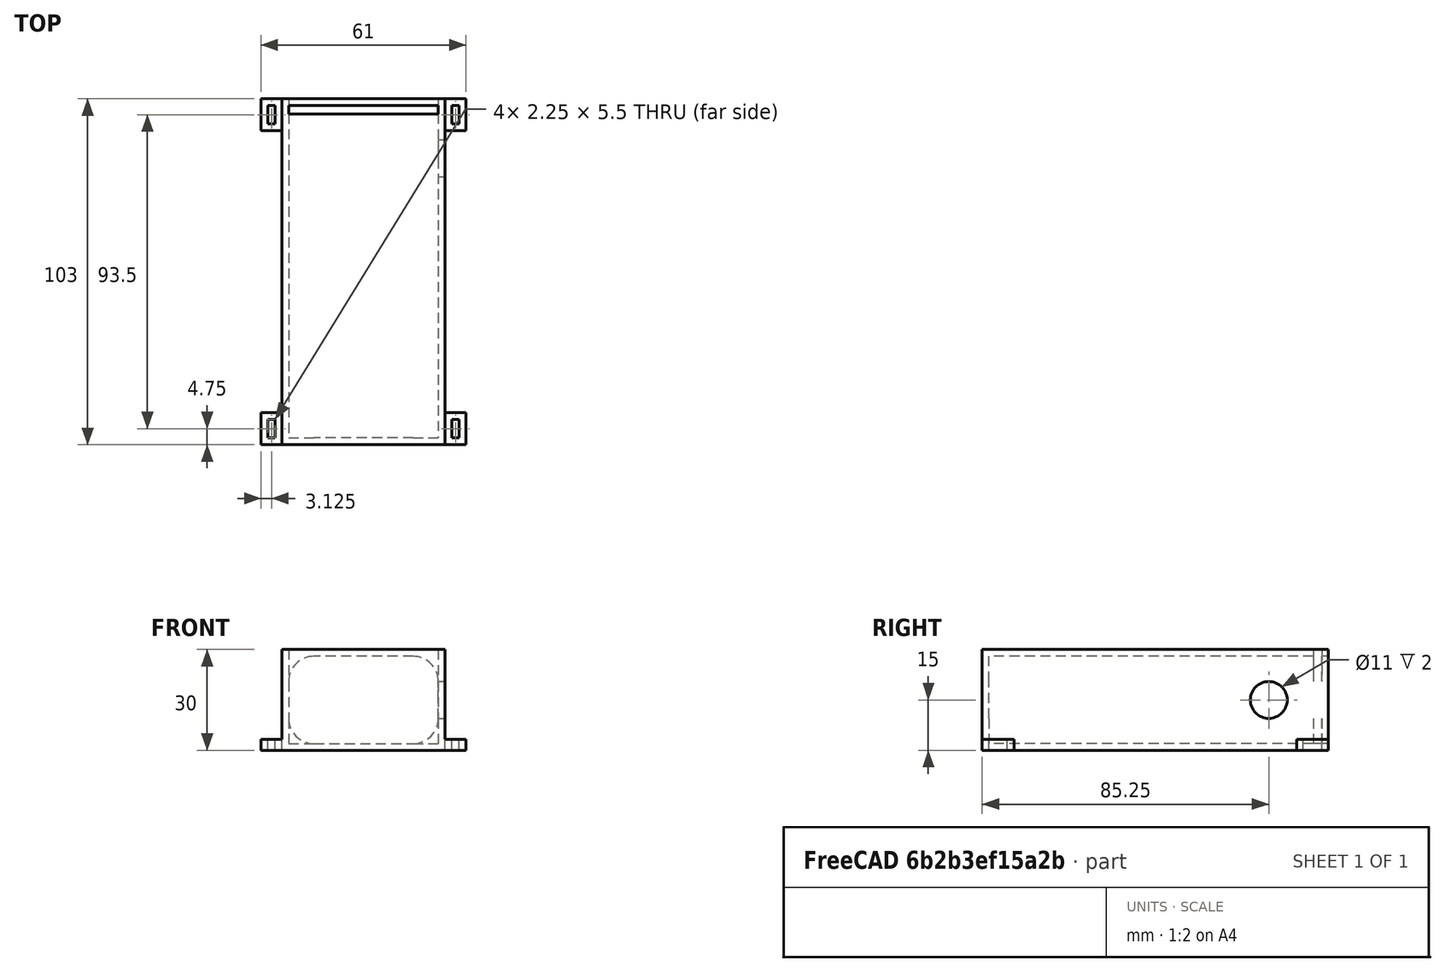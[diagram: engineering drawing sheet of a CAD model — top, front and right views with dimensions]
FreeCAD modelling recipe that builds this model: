
FCSTD DOCUMENT  (FreeCAD 0.19R)
Label: power-bank-mount-base
License: All rights reserved
LicenseURL: http://en.wikipedia.org/wiki/All_rights_reserved
objects: Sketcher::SketchObject×5, PartDesign::Pocket×3, PartDesign::Pad×2, PartDesign::Body×1, Mesh::Feature×1
note: 16 computed .brp shape members not serialized (recipe doc carries the construction recipe); baked Part::Feature solids carry a one-line shape summary decoded from their .brp

FEATURE [Sketcher::SketchObject] Sketch
  FullyConstrained = true
  MapMode = 5
  Support = -> [XY_Plane]
  sketch-geometry (4):
    g0: LineSegment StartX=0 StartY=0 StartZ=0 EndX=48.5 EndY=0 EndZ=0
    g1: LineSegment StartX=48.5 StartY=0 StartZ=0 EndX=48.5 EndY=103 EndZ=0
    g2: LineSegment StartX=48.5 StartY=103 StartZ=0 EndX=0 EndY=103 EndZ=0
    g3: LineSegment StartX=0 StartY=103 StartZ=0 EndX=0 EndY=0 EndZ=0
  constraints (11):
    c: Coincident(g0,g1)
    c: Coincident(g1,g2)
    c: Coincident(g2,g3)
    c: Coincident(g3,g0)
    c: Horizontal(g0)
    c: Horizontal(g2)
    c: Vertical(g1)
    c: Vertical(g3)
    c: Coincident(g0,g-1)
    c: DistanceX(g2,g2) = 48.5
    c: DistanceY(g1,g1) = 103
FEATURE [PartDesign::Pad] Pad
  Direction = (1,1,1)
  Length = 30
  Length2 = 100
  Profile = -> Sketch
  Type = 0
FEATURE [Sketcher::SketchObject] Sketch001
  FullyConstrained = true
  MapMode = 5
  Placement = pos=(0,103,0) rot=(0,0.707107,0.707107;3.14159rad)
  Support = -> [Pad]
  sketch-geometry (14):
    g0: LineSegment StartX=-39 StartY=28 StartZ=0 EndX=-9.5 EndY=28 EndZ=0
    g1: LineSegment StartX=-2 StartY=20.5 StartZ=0 EndX=-2 EndY=9.5 EndZ=0
    g2: LineSegment StartX=-9.5 StartY=2 StartZ=0 EndX=-39 EndY=2 EndZ=0
    g3: LineSegment StartX=-46.5 StartY=9.5 StartZ=0 EndX=-46.5 EndY=20.5 EndZ=0
    g4: ArcOfCircle CenterX=-39 CenterY=20.5 CenterZ=0 NormalX=0 NormalY=0 NormalZ=1 AngleXU=0 Radius=7.5 StartAngle=1.5708 EndAngle=3.14159
    g5: ArcOfCircle CenterX=-9.5 CenterY=20.5 CenterZ=0 NormalX=0 NormalY=0 NormalZ=1 AngleXU=0 Radius=7.5 StartAngle=0 EndAngle=1.5708
    g6: ArcOfCircle CenterX=-9.5 CenterY=9.5 CenterZ=0 NormalX=0 NormalY=0 NormalZ=1 AngleXU=0 Radius=7.5 StartAngle=4.71239 EndAngle=6.28319
    g7: ArcOfCircle CenterX=-39 CenterY=9.5 CenterZ=0 NormalX=0 NormalY=0 NormalZ=1 AngleXU=0 Radius=7.5 StartAngle=3.14159 EndAngle=4.71239
    g8: LineSegment StartX=0 StartY=0 StartZ=0 EndX=-48.5 EndY=0 EndZ=0
    g9: LineSegment StartX=-48.5 StartY=0 StartZ=0 EndX=-48.5 EndY=30 EndZ=0
    g10: LineSegment StartX=-48.5 StartY=30 StartZ=0 EndX=0 EndY=30 EndZ=0
    g11: LineSegment StartX=0 StartY=30 StartZ=0 EndX=0 EndY=0 EndZ=0
    g12: LineSegment StartX=-24.25 StartY=28 StartZ=0 EndX=-24.25 EndY=30 EndZ=0
    g13: LineSegment StartX=-2 StartY=15 StartZ=0 EndX=0 EndY=15 EndZ=0
  constraints (35):
    c: Horizontal(g0)
    c: Horizontal(g2)
    c: Vertical(g1)
    c: Vertical(g3)
    c: Tangent(g0,g4) = 1.5708
    c: Tangent(g3,g4) = 1.5708
    c: Tangent(g0,g5) = 1.5708
    c: Tangent(g1,g5) = 1.5708
    c: Tangent(g1,g6) = 1.5708
    c: Tangent(g2,g6) = 1.5708
    c: Tangent(g2,g7) = 1.5708
    c: Tangent(g3,g7) = 1.5708
    c: DistanceY(g2,g0) = 26
    c: Coincident(g8,g9)
    c: Coincident(g9,g10)
    c: Coincident(g10,g11)
    c: Coincident(g11,g8)
    c: Horizontal(g8)
    c: Horizontal(g10)
    c: Vertical(g9)
    c: Vertical(g11)
    c: Coincident(g8,g-1)
    c: DistanceX(g10,g10) = 48.5
    c: DistanceY(g9,g9) = 30
    c: Distance(g0,g5) = 7.5
    c: Equal(g5,g4)
    c: Equal(g4,g7)
    c: Equal(g7,g6)
    c: Vertical(g12)
    c: Horizontal(g13)
    c: DistanceX(g3,g1) = 44.5
    c: Symmetric(g10,g9,g12)
    c: Symmetric(g0,g0,g12)
    c: Symmetric(g1,g1,g13)
    c: Symmetric(g-1,g10,g13)
FEATURE [PartDesign::Pocket] Pocket
  BaseFeature = -> Pad
  Length = 101
  Length2 = 100
  Profile = -> Sketch001
  Type = 0
FEATURE [Sketcher::SketchObject] Sketch002
  FullyConstrained = true
  MapMode = 5
  Placement = pos=(0,0,30) rot=(0,0,1;0rad)
  Support = -> [Pocket]
  sketch-geometry (9):
    g0: LineSegment StartX=0 StartY=0 StartZ=0 EndX=48.5 EndY=0 EndZ=0
    g1: LineSegment StartX=48.5 StartY=0 StartZ=0 EndX=48.5 EndY=103 EndZ=0
    g2: LineSegment StartX=48.5 StartY=103 StartZ=0 EndX=0 EndY=103 EndZ=0
    g3: LineSegment StartX=0 StartY=103 StartZ=0 EndX=0 EndY=0 EndZ=0
    g4: LineSegment StartX=2 StartY=101 StartZ=0 EndX=46.5 EndY=101 EndZ=0
    g5: LineSegment StartX=46.5 StartY=101 StartZ=0 EndX=46.5 EndY=98.5 EndZ=0
    g6: LineSegment StartX=46.5 StartY=98.5 StartZ=0 EndX=2 EndY=98.5 EndZ=0
    g7: LineSegment StartX=2 StartY=98.5 StartZ=0 EndX=2 EndY=101 EndZ=0
    g8: LineSegment StartX=24.25 StartY=101 StartZ=0 EndX=24.25 EndY=103 EndZ=0
  constraints (25):
    c: Coincident(g0,g1)
    c: Coincident(g1,g2)
    c: Coincident(g2,g3)
    c: Coincident(g3,g0)
    c: Horizontal(g0)
    c: Horizontal(g2)
    c: Vertical(g1)
    c: Vertical(g3)
    c: Coincident(g0,g-1)
    c: Coincident(g4,g5)
    c: Coincident(g5,g6)
    c: Coincident(g6,g7)
    c: Coincident(g7,g4)
    c: Horizontal(g4)
    c: Horizontal(g6)
    c: Vertical(g5)
    c: Vertical(g7)
    c: Vertical(g8)
    c: DistanceX(g0,g0) = 48.5
    c: DistanceY(g1,g1) = 103
    c: DistanceX(g6,g6) = 44.5
    c: DistanceY(g5,g5) = 2.5
    c: Symmetric(g4,g4,g8)
    c: Symmetric(g1,g2,g8)
    c: DistanceY(g8,g8) = 2
FEATURE [PartDesign::Pocket] Pocket001
  BaseFeature = -> Pocket
  Length = 28
  Length2 = 100
  Profile = -> Sketch002
  Type = 0
FEATURE [Sketcher::SketchObject] Sketch003
  FullyConstrained = true
  MapMode = 5
  Support = -> [XY_Plane]
  sketch-geometry (44):
    g0: LineSegment StartX=0 StartY=0 StartZ=0 EndX=48.5 EndY=0 EndZ=0
    g1: LineSegment StartX=48.5 StartY=0 StartZ=0 EndX=48.5 EndY=103 EndZ=0
    g2: LineSegment StartX=48.5 StartY=103 StartZ=0 EndX=0 EndY=103 EndZ=0
    g3: LineSegment StartX=0 StartY=103 StartZ=0 EndX=0 EndY=0 EndZ=0
    g4: LineSegment StartX=0 StartY=103 StartZ=0 EndX=-6.25 EndY=103 EndZ=0
    g5: LineSegment StartX=-6.25 StartY=103 StartZ=0 EndX=-6.25 EndY=93.5 EndZ=0
    g6: LineSegment StartX=-6.25 StartY=93.5 StartZ=0 EndX=0 EndY=93.5 EndZ=0
    g7: LineSegment StartX=0 StartY=93.5 StartZ=0 EndX=0 EndY=103 EndZ=0
    g8: LineSegment StartX=48.5 StartY=103 StartZ=0 EndX=54.75 EndY=103 EndZ=0
    g9: LineSegment StartX=54.75 StartY=103 StartZ=0 EndX=54.75 EndY=93.5 EndZ=0
    g10: LineSegment StartX=54.75 StartY=93.5 StartZ=0 EndX=48.5 EndY=93.5 EndZ=0
    g11: LineSegment StartX=48.5 StartY=93.5 StartZ=0 EndX=48.5 EndY=103 EndZ=0
    g12: LineSegment StartX=0 StartY=0 StartZ=0 EndX=-6.25 EndY=0 EndZ=0
    g13: LineSegment StartX=-6.25 StartY=0 StartZ=0 EndX=-6.25 EndY=9.5 EndZ=0
    g14: LineSegment StartX=-6.25 StartY=9.5 StartZ=0 EndX=0 EndY=9.5 EndZ=0
    g15: LineSegment StartX=0 StartY=9.5 StartZ=0 EndX=0 EndY=0 EndZ=0
    g16: LineSegment StartX=48.5 StartY=0 StartZ=0 EndX=54.75 EndY=0 EndZ=0
    g17: LineSegment StartX=54.75 StartY=0 StartZ=0 EndX=54.75 EndY=9.5 EndZ=0
    g18: LineSegment StartX=54.75 StartY=9.5 StartZ=0 EndX=48.5 EndY=9.5 EndZ=0
    g19: LineSegment StartX=48.5 StartY=9.5 StartZ=0 EndX=48.5 EndY=0 EndZ=0
    g20: LineSegment StartX=-4.25 StartY=101 StartZ=0 EndX=-2 EndY=101 EndZ=0
    g21: LineSegment StartX=-2 StartY=101 StartZ=0 EndX=-2 EndY=95.5 EndZ=0
    g22: LineSegment StartX=-2 StartY=95.5 StartZ=0 EndX=-4.25 EndY=95.5 EndZ=0
    g23: LineSegment StartX=-4.25 StartY=95.5 StartZ=0 EndX=-4.25 EndY=101 EndZ=0
    g24: LineSegment StartX=50.5 StartY=101 StartZ=0 EndX=52.75 EndY=101 EndZ=0
    g25: LineSegment StartX=52.75 StartY=101 StartZ=0 EndX=52.75 EndY=95.5 EndZ=0
    g26: LineSegment StartX=52.75 StartY=95.5 StartZ=0 EndX=50.5 EndY=95.5 EndZ=0
    g27: LineSegment StartX=50.5 StartY=95.5 StartZ=0 EndX=50.5 EndY=101 EndZ=0
    g28: LineSegment StartX=-4.25 StartY=7.5 StartZ=0 EndX=-2 EndY=7.5 EndZ=0
    g29: LineSegment StartX=-2 StartY=7.5 StartZ=0 EndX=-2 EndY=2 EndZ=0
    g30: LineSegment StartX=-2 StartY=2 StartZ=0 EndX=-4.25 EndY=2 EndZ=0
    g31: LineSegment StartX=-4.25 StartY=2 StartZ=0 EndX=-4.25 EndY=7.5 EndZ=0
    g32: LineSegment StartX=52.75 StartY=7.5 StartZ=0 EndX=50.5 EndY=7.5 EndZ=0
    g33: LineSegment StartX=50.5 StartY=7.5 StartZ=0 EndX=50.5 EndY=2 EndZ=0
    g34: LineSegment StartX=50.5 StartY=2 StartZ=0 EndX=52.75 EndY=2 EndZ=0
    g35: LineSegment StartX=52.75 StartY=2 StartZ=0 EndX=52.75 EndY=7.5 EndZ=0
    g36: LineSegment StartX=-3.125 StartY=101 StartZ=0 EndX=-3.125 EndY=103 EndZ=0
    g37: LineSegment StartX=-4.25 StartY=98.25 StartZ=0 EndX=-6.25 EndY=98.25 EndZ=0
    g38: LineSegment StartX=51.625 StartY=101 StartZ=0 EndX=51.625 EndY=103 EndZ=0
    g39: LineSegment StartX=52.75 StartY=98.25 StartZ=0 EndX=54.75 EndY=98.25 EndZ=0
    g40: LineSegment StartX=-3.125 StartY=7.5 StartZ=0 EndX=-3.125 EndY=9.5 EndZ=0
    g41: LineSegment StartX=-4.25 StartY=4.75 StartZ=0 EndX=-6.25 EndY=4.75 EndZ=0
    g42: LineSegment StartX=51.625 StartY=7.5 StartZ=0 EndX=51.625 EndY=9.5 EndZ=0
    g43: LineSegment StartX=52.75 StartY=4.75 StartZ=0 EndX=54.75 EndY=4.75 EndZ=0
  constraints (119):
    c: Coincident(g0,g1)
    c: Coincident(g1,g2)
    c: Coincident(g2,g3)
    c: Coincident(g3,g0)
    c: Horizontal(g0)
    c: Horizontal(g2)
    c: Vertical(g1)
    c: Vertical(g3)
    c: Coincident(g0,g-1)
    c: DistanceX(g2,g2) = 48.5
    c: DistanceY(g1,g1) = 103
    c: Coincident(g4,g5)
    c: Coincident(g5,g6)
    c: Coincident(g6,g7)
    c: Coincident(g7,g4)
    c: Horizontal(g4)
    c: Horizontal(g6)
    c: Vertical(g5)
    c: Vertical(g7)
    c: Coincident(g4,g2)
    c: Coincident(g8,g9)
    c: Coincident(g9,g10)
    c: Coincident(g10,g11)
    c: Coincident(g11,g8)
    c: Horizontal(g8)
    c: Horizontal(g10)
    c: Vertical(g9)
    c: Vertical(g11)
    c: Coincident(g8,g1)
    c: Coincident(g12,g13)
    c: Coincident(g13,g14)
    c: Coincident(g14,g15)
    c: Coincident(g15,g12)
    c: Horizontal(g12)
    c: Horizontal(g14)
    c: Vertical(g13)
    c: Vertical(g15)
    c: Coincident(g12,g-1)
    c: Coincident(g16,g17)
    c: Coincident(g17,g18)
    c: Coincident(g18,g19)
    c: Coincident(g19,g16)
    c: Horizontal(g16)
    c: Horizontal(g18)
    c: Vertical(g17)
    c: Vertical(g19)
    c: Coincident(g16,g0)
    c: Coincident(g20,g21)
    c: Coincident(g21,g22)
    c: Coincident(g22,g23)
    c: Coincident(g23,g20)
    c: Horizontal(g20)
    c: Horizontal(g22)
    c: Vertical(g21)
    c: Vertical(g23)
    c: Coincident(g24,g25)
    c: Coincident(g25,g26)
    c: Coincident(g26,g27)
    c: Coincident(g27,g24)
    c: Horizontal(g24)
    c: Horizontal(g26)
    c: Vertical(g25)
    c: Vertical(g27)
    c: Coincident(g28,g29)
    c: Coincident(g29,g30)
    c: Coincident(g30,g31)
    c: Coincident(g31,g28)
    c: Horizontal(g28)
    c: Horizontal(g30)
    c: Vertical(g29)
    c: Vertical(g31)
    c: Coincident(g32,g33)
    c: Coincident(g33,g34)
    c: Coincident(g34,g35)
    c: Coincident(g35,g32)
    c: Horizontal(g32)
    c: Horizontal(g34)
    c: Vertical(g33)
    c: Vertical(g35)
    c: Vertical(g36)
    c: Horizontal(g37)
    c: Vertical(g38)
    c: Vertical(g40)
    c: Horizontal(g41)
    c: Vertical(g42)
    c: Symmetric(g20,g20,g36)
    c: Symmetric(g4,g4,g36)
    c: Symmetric(g20,g22,g37)
    c: Symmetric(g5,g4,g37)
    c: Symmetric(g24,g24,g38)
    c: Symmetric(g25,g24,g39)
    c: Symmetric(g8,g8,g38)
    c: Symmetric(g9,g8,g39)
    c: Symmetric(g28,g28,g40)
    c: Symmetric(g14,g13,g40)
    c: Symmetric(g30,g28,g41)
    c: Symmetric(g12,g13,g41)
    c: Symmetric(g32,g32,g42)
    c: Symmetric(g17,g18,g42)
    c: Equal(g4,g8)
    c: Equal(g8,g14)
    c: Equal(g14,g18)
    c: Equal(g5,g9)
    c: Equal(g9,g13)
    c: Equal(g13,g17)
    c: Horizontal(g39)
    c: Equal(g20,g24)
    c: Equal(g24,g28)
    c: Equal(g28,g32)
    c: Equal(g21,g27)
    c: Equal(g27,g29)
    c: Equal(g29,g33)
    c: Horizontal(g43)
    c: Symmetric(g34,g32,g43)
    c: Symmetric(g16,g17,g43)
    c: DistanceX(g22,g22) = 2.25
    c: DistanceY(g21,g21) = 5.5
    c: DistanceX(g4,g20) = 2
    c: DistanceY(g20,g4) = 2
FEATURE [PartDesign::Pad] Pad001
  BaseFeature = -> Pocket001
  Direction = (1,1,1)
  Length = 3.25
  Length2 = 100
  Profile = -> Sketch003
  Type = 0
FEATURE [Sketcher::SketchObject] Sketch004
  FullyConstrained = true
  MapMode = 5
  Placement = pos=(48.5,0,0) rot=(0.57735,0.57735,0.57735;2.0944rad)
  Support = -> [Pad001]
  sketch-geometry (11):
    g0: LineSegment StartX=0 StartY=0 StartZ=0 EndX=103 EndY=0 EndZ=0
    g1: LineSegment StartX=103 StartY=0 StartZ=0 EndX=103 EndY=30 EndZ=0
    g2: LineSegment StartX=103 StartY=30 StartZ=0 EndX=0 EndY=30 EndZ=0
    g3: LineSegment StartX=0 StartY=30 StartZ=0 EndX=0 EndY=0 EndZ=0
    g4: Circle CenterX=85.25 CenterY=15 CenterZ=0 NormalX=0 NormalY=0 NormalZ=1 AngleXU=0 Radius=5.5
    g5: LineSegment StartX=2.25 StartY=27.75 StartZ=0 EndX=98.25 EndY=27.75 EndZ=0
    g6: LineSegment StartX=98.25 StartY=27.75 StartZ=0 EndX=98.25 EndY=2.25 EndZ=0
    g7: LineSegment StartX=98.25 StartY=2.25 StartZ=0 EndX=2.25 EndY=2.25 EndZ=0
    g8: LineSegment StartX=2.25 StartY=2.25 StartZ=0 EndX=2.25 EndY=27.75 EndZ=0
    g9: LineSegment StartX=0 StartY=15 StartZ=0 EndX=2.25 EndY=15 EndZ=0
    g10: LineSegment StartX=85.25 StartY=15 StartZ=0 EndX=98.25 EndY=15 EndZ=0
  constraints (30):
    c: Coincident(g0,g1)
    c: Coincident(g1,g2)
    c: Coincident(g2,g3)
    c: Coincident(g3,g0)
    c: Horizontal(g0)
    c: Horizontal(g2)
    c: Vertical(g1)
    c: Vertical(g3)
    c: Coincident(g0,g-1)
    c: DistanceX(g2,g2) = 103
    c: DistanceY(g3,g3) = 30
    c: Diameter(g4) = 11
    c: Coincident(g5,g6)
    c: Coincident(g6,g7)
    c: Coincident(g7,g8)
    c: Coincident(g8,g5)
    c: Horizontal(g5)
    c: Horizontal(g7)
    c: Vertical(g6)
    c: Vertical(g8)
    c: DistanceX(g7,g7) = 96
    c: DistanceY(g6,g6) = 25.5
    c: Horizontal(g9)
    c: DistanceX(g9,g9) = 2.25
    c: Symmetric(g-1,g2,g9)
    c: Symmetric(g7,g5,g9)
    c: Coincident(g10,g4)
    c: Horizontal(g10)
    c: Symmetric(g6,g5,g10)
    c: DistanceX(g10,g10) = 13
FEATURE [PartDesign::Pocket] Pocket002
  BaseFeature = -> Pad001
  Length = 5
  Length2 = 100
  Profile = -> Sketch004
  Type = 2
FEATURE [PartDesign::Body] Body
  Group = -> [Sketch,Pad,Sketch001,Pocket,Sketch002,Pocket001,Sketch003,Pad001,Sketch004,Pocket002]
  Origin = -> Origin
  Tip = -> Pocket002
FEATURE [Mesh::Feature] Mesh  label="Body (Meshed)"
